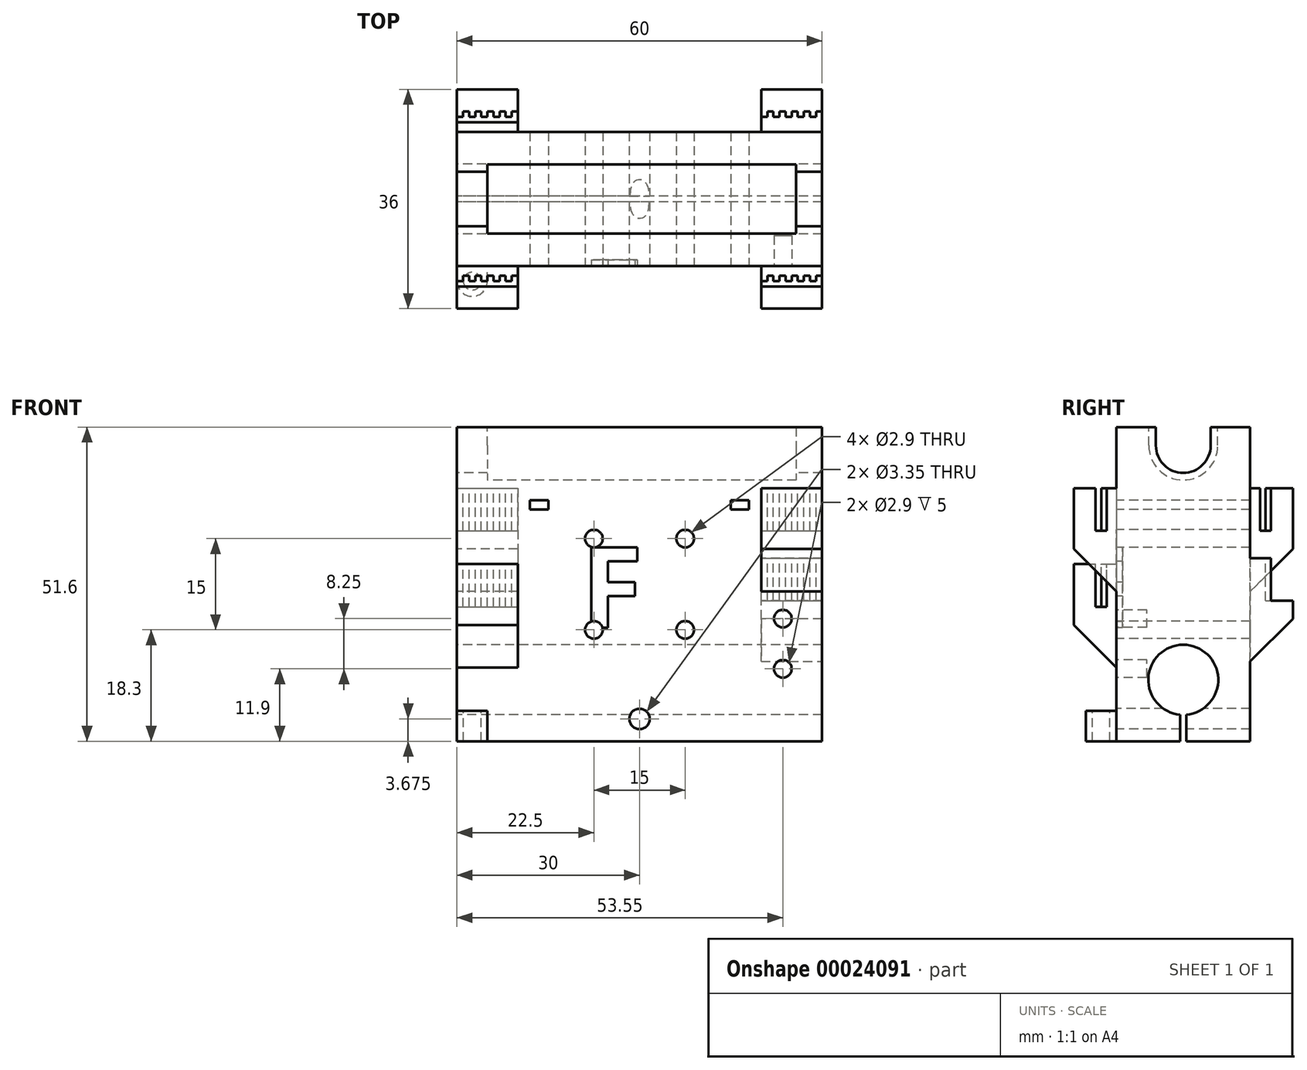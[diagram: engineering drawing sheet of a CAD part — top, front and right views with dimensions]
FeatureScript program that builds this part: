
annotation { "Feature Type Name" : "Feature", "Feature Type Description" : "" }
export const myFeature = defineFeature(function(context is Context, id is Id, definition is map)
    precondition{}
    {
        {
            var Q0;
            Q0=qCreatedBy(makeId("Top.planeOp"),FACE);
            var sketch = newSketch(context, id + "F0", { "sketchPlane" : qUnion([Q0])});
            skLineSegment(sketch, "E0.bottom", {"start": v(0, 0) * mm, "end": v(60, 0) * mm});
            skLineSegment(sketch, "E0.top", {"start": v(0, 22) * mm, "end": v(60, 22) * mm});
            skLineSegment(sketch, "E0.left", {"start": v(0, 0) * mm, "end": v(0, 22) * mm});
            skLineSegment(sketch, "E0.right", {"start": v(60, 0) * mm, "end": v(60, 22) * mm});
            skSolve(sketch);
        }
        {
            var Q0;
            Q0=qSketchRegion(id+"F0",true);
            extrude(context, id + "F1", {"entities" : qUnion([Q0]), "depth" : 51.6 * mm});
        }
        {
            var Q0;
            Q0=makeQuery(id+"F1.opExtrude","SWEPT_FACE",FACE,{"disambiguationData":[OSD([sQuery(id+"F0.wireOp",EDGE,"E0.left")])]});
            var sketch = newSketch(context, id + "F2", { "sketchPlane" : qUnion([Q0])});
            skCircle(sketch, "E1", {"center": v(-11, 10.1) * mm, "radius": 5.75 * mm});
            skCircle(sketch, "E2", {"center": v(-11, 48.6) * mm, "radius": 4.5 * mm});
            skLineSegment(sketch, "E3", {"start": v(-22, 48.6) * mm, "end": v(0, 48.6) * mm, "construction": true});
            skLineSegment(sketch, "E4", {"start": v(-15.5, 51.6) * mm, "end": v(-15.5, 48.6) * mm});
            skLineSegment(sketch, "E5", {"start": v(-6.5, 51.6) * mm, "end": v(-6.5, 48.6) * mm});
            skLineSegment(sketch, "E6", {"start": v(-22, 10.1) * mm, "end": v(0, 10.1) * mm, "construction": true});
            skLineSegment(sketch, "E7", {"start": v(-11, 10.1) * mm, "end": v(-11, 0) * mm, "construction": true});
            skLineSegment(sketch, "E8", {"start": v(-11, 0) * mm, "end": v(-11.5, 0) * mm});
            skLineSegment(sketch, "E9", {"start": v(-11.5, 0) * mm, "end": v(-11.5, 4.37) * mm});
            skLineSegment(sketch, "E10", {"start": v(-11.5, 4.37) * mm, "end": v(-10.5, 4.37) * mm});
            skLineSegment(sketch, "E11", {"start": v(-10.5, 4.37) * mm, "end": v(-10.5, 0) * mm});
            skLineSegment(sketch, "E12", {"start": v(-10.5, 0) * mm, "end": v(-11, 0) * mm});
            skLineSegment(sketch, "E13", {"start": v(-11, 15.85) * mm, "end": v(-11, 19.08) * mm});
            skLineSegment(sketch, "E14", {"start": v(-11, 19.08) * mm, "end": v(-7.6, 14.73) * mm});
            skLineSegment(sketch, "E15", {"start": v(-11, 19.08) * mm, "end": v(-14.4, 14.73) * mm});
            skCircle(sketch, "E16", {"center": v(-11, 48.6) * mm, "radius": 5.68 * mm});
            skLineSegment(sketch, "E17", {"start": v(-5.32, 48.6) * mm, "end": v(-5.32, 51.6) * mm});
            skLineSegment(sketch, "E18", {"start": v(-16.67, 48.6) * mm, "end": v(-16.67, 51.6) * mm});
            skSolve(sketch);
        }
        {
            var Q0;
            {var subQ0=sQuery(id+"F2.wireOp",EDGE,"E14");var subQ1=sQuery(id+"F2.wireOp",EDGE,"E1");var subQ3=makeQuery(id+"F2.imprint","INTERSECT",VERTEX,{"disambiguationData":[OD(0.0)],"derivedFrom":[subQ1,subQ0]});Q0=makeQuery(id+"F2.imprint","IMPRINT",FACE,{"disambiguationData":[TD([[makeQuery(id+"F2.imprint","IMPRINT",EDGE,{"disambiguationData":[TD([[subQ3,-1.0]])],"derivedFrom":subQ1}),1.0]])]});}
            var Q1;
            {var subQ0=sQuery(id+"F2.wireOp",EDGE,"E15");var subQ1=sQuery(id+"F2.wireOp",EDGE,"E1");var subQ3=makeQuery(id+"F2.imprint","INTERSECT",VERTEX,{"disambiguationData":[OD(0.0)],"derivedFrom":[subQ1,subQ0]});Q1=makeQuery(id+"F2.imprint","IMPRINT",FACE,{"disambiguationData":[TD([[makeQuery(id+"F2.imprint","IMPRINT",EDGE,{"disambiguationData":[TD([[subQ3,1.0]])],"derivedFrom":subQ1}),1.0]])]});}
            var Q2;
            Q2=makeQuery(id+"F2.imprint","IMPRINT",FACE,{"disambiguationData":[TD([[makeQuery(id+"F2.imprint","IMPRINT",EDGE,{"derivedFrom":sQuery(id+"F2.wireOp",EDGE,"E8")}),-1.0]])]});
            var Q3;
            {var subQ0=sQuery(id+"F2.wireOp",EDGE,"E10");Q3=makeQuery(id+"F2.imprint","IMPRINT",FACE,{"disambiguationData":[TD([[makeQuery(id+"F2.imprint","IMPRINT",EDGE,{"derivedFrom":subQ0}),-1.0]])]});}
            var Q4;
            {var subQ7=sQuery(id+"F2.wireOp",EDGE,"E10");Q4=makeQuery(id+"F2.imprint","IMPRINT",FACE,{"disambiguationData":[TD([[makeQuery(id+"F2.imprint","IMPRINT",EDGE,{"derivedFrom":subQ7}),1.0]])]});}
            var Q5;
            {var subQ3=sQuery(id+"F2.wireOp",EDGE,"E5");Q5=makeQuery(id+"F2.imprint","IMPRINT",FACE,{"disambiguationData":[TD([[makeQuery(id+"F2.imprint","IMPRINT",EDGE,{"derivedFrom":subQ3}),-1.0]])]});}
            var Q6;
            {var subQ0=sQuery(id+"F2.wireOp",EDGE,"E4");Q6=makeQuery(id+"F2.imprint","IMPRINT",FACE,{"disambiguationData":[TD([[makeQuery(id+"F2.imprint","IMPRINT",EDGE,{"derivedFrom":subQ0}),1.0]])]});}
            var Q7;
            {var subQ0=sQuery(id+"F2.wireOp",EDGE,"E4");Q7=makeQuery(id+"F2.imprint","IMPRINT",FACE,{"disambiguationData":[TD([[makeQuery(id+"F2.imprint","IMPRINT",EDGE,{"derivedFrom":subQ0}),1.0]])]});}
            var Q8;
            {var subQ3=sQuery(id+"F2.wireOp",EDGE,"E5");Q8=makeQuery(id+"F2.imprint","IMPRINT",FACE,{"disambiguationData":[TD([[makeQuery(id+"F2.imprint","IMPRINT",EDGE,{"derivedFrom":subQ3}),-1.0]])]});}
            var Q9;
            {var subQ1=sQuery(id+"F2.wireOp",EDGE,"E2");var subQ4=makeQuery(id+"F2.imprint","INTERSECT",VERTEX,{"derivedFrom":[subQ1,sQuery(id+"F2.wireOp",EDGE,"E5")]});Q9=makeQuery(id+"F2.imprint","IMPRINT",FACE,{"disambiguationData":[TD([[makeQuery(id+"F2.imprint","IMPRINT",EDGE,{"disambiguationData":[TD([[subQ4,-1.0]])],"derivedFrom":subQ1}),1.0]])]});}
            extrude(context, id + "F3", {"entities" : qUnion([Q0, Q1, Q2, Q3, Q4, Q5, Q6, Q7, Q8, Q9]), "operationType" : NewBodyOperationType.REMOVE, "endBound" : BoundingType.THROUGH_ALL, "oppositeDirection" : true, "depth" : 25 * mm});
        }
        {
            var Q0;
            {var subQ3=sQuery(id+"F2.wireOp",EDGE,"E4");Q0=makeQuery(id+"F2.imprint","IMPRINT",FACE,{"disambiguationData":[TD([[makeQuery(id+"F2.imprint","IMPRINT",EDGE,{"derivedFrom":subQ3}),-1.0]])]});}
            var Q1;
            {var subQ3=sQuery(id+"F2.wireOp",EDGE,"E18");Q1=makeQuery(id+"F2.imprint","IMPRINT",FACE,{"disambiguationData":[TD([[makeQuery(id+"F2.imprint","IMPRINT",EDGE,{"derivedFrom":subQ3}),-1.0]])]});}
            var Q2;
            {var subQ3=sQuery(id+"F2.wireOp",EDGE,"E17");Q2=makeQuery(id+"F2.imprint","IMPRINT",FACE,{"disambiguationData":[TD([[makeQuery(id+"F2.imprint","IMPRINT",EDGE,{"derivedFrom":subQ3}),1.0]])]});}
            extrude(context, id + "F4", {"entities" : qUnion([Q0, Q1, Q2]), "operationType" : NewBodyOperationType.REMOVE, "oppositeDirection" : true, "depth" : 55.75 * mm});
        }
        {
            var Q0;
            {var subQ3=sQuery(id+"F2.wireOp",EDGE,"E4");Q0=makeQuery(id+"F2.imprint","IMPRINT",FACE,{"disambiguationData":[TD([[makeQuery(id+"F2.imprint","IMPRINT",EDGE,{"derivedFrom":subQ3}),-1.0]])]});}
            var Q1;
            {var subQ3=sQuery(id+"F2.wireOp",EDGE,"E18");Q1=makeQuery(id+"F2.imprint","IMPRINT",FACE,{"disambiguationData":[TD([[makeQuery(id+"F2.imprint","IMPRINT",EDGE,{"derivedFrom":subQ3}),-1.0]])]});}
            var Q2;
            {var subQ3=sQuery(id+"F2.wireOp",EDGE,"E17");Q2=makeQuery(id+"F2.imprint","IMPRINT",FACE,{"disambiguationData":[TD([[makeQuery(id+"F2.imprint","IMPRINT",EDGE,{"derivedFrom":subQ3}),1.0]])]});}
            extrude(context, id + "F5", {"entities" : qUnion([Q0, Q1, Q2]), "operationType" : NewBodyOperationType.ADD, "oppositeDirection" : true, "depth" : 32.75 * mm});
        }
        {
            var Q0;
            {var subQ3=sQuery(id+"F2.wireOp",EDGE,"E4");Q0=makeQuery(id+"F2.imprint","IMPRINT",FACE,{"disambiguationData":[TD([[makeQuery(id+"F2.imprint","IMPRINT",EDGE,{"derivedFrom":subQ3}),-1.0]])]});}
            var Q1;
            {var subQ3=sQuery(id+"F2.wireOp",EDGE,"E18");Q1=makeQuery(id+"F2.imprint","IMPRINT",FACE,{"disambiguationData":[TD([[makeQuery(id+"F2.imprint","IMPRINT",EDGE,{"derivedFrom":subQ3}),-1.0]])]});}
            var Q2;
            {var subQ3=sQuery(id+"F2.wireOp",EDGE,"E17");Q2=makeQuery(id+"F2.imprint","IMPRINT",FACE,{"disambiguationData":[TD([[makeQuery(id+"F2.imprint","IMPRINT",EDGE,{"derivedFrom":subQ3}),1.0]])]});}
            extrude(context, id + "F6", {"entities" : qUnion([Q0, Q1, Q2]), "operationType" : NewBodyOperationType.REMOVE, "oppositeDirection" : true, "depth" : 34.25 * mm});
        }
        {
            var Q0;
            {var subQ3=sQuery(id+"F2.wireOp",EDGE,"E4");Q0=makeQuery(id+"F2.imprint","IMPRINT",FACE,{"disambiguationData":[TD([[makeQuery(id+"F2.imprint","IMPRINT",EDGE,{"derivedFrom":subQ3}),-1.0]])]});}
            var Q1;
            {var subQ3=sQuery(id+"F2.wireOp",EDGE,"E18");Q1=makeQuery(id+"F2.imprint","IMPRINT",FACE,{"disambiguationData":[TD([[makeQuery(id+"F2.imprint","IMPRINT",EDGE,{"derivedFrom":subQ3}),-1.0]])]});}
            var Q2;
            {var subQ3=sQuery(id+"F2.wireOp",EDGE,"E17");Q2=makeQuery(id+"F2.imprint","IMPRINT",FACE,{"disambiguationData":[TD([[makeQuery(id+"F2.imprint","IMPRINT",EDGE,{"derivedFrom":subQ3}),1.0]])]});}
            extrude(context, id + "F7", {"entities" : qUnion([Q0, Q1, Q2]), "operationType" : NewBodyOperationType.ADD, "oppositeDirection" : true, "depth" : 5 * mm});
        }
        {
            var Q0;
            Q0=makeQuery(id+"F1.opExtrude","SWEPT_FACE",FACE,{"disambiguationData":[OSD([sQuery(id+"F0.wireOp",EDGE,"E0.bottom")])]});
            var sketch = newSketch(context, id + "F8", { "sketchPlane" : qUnion([Q0])});
            skLineSegment(sketch, "E19.bottom", {"start": v(0, 29.1) * mm, "end": v(10, 29.1) * mm});
            skLineSegment(sketch, "E19.top", {"start": v(0, 9.1) * mm, "end": v(10, 9.1) * mm});
            skLineSegment(sketch, "E19.left", {"start": v(0, 29.1) * mm, "end": v(0, 9.1) * mm});
            skLineSegment(sketch, "E19.right", {"start": v(10, 29.1) * mm, "end": v(10, 9.1) * mm});
            skLineSegment(sketch, "E20.bottom", {"start": v(60, 41.6) * mm, "end": v(50, 41.6) * mm});
            skLineSegment(sketch, "E20.top", {"start": v(60, 21.6) * mm, "end": v(50, 21.6) * mm});
            skLineSegment(sketch, "E20.left", {"start": v(60, 41.6) * mm, "end": v(60, 21.6) * mm});
            skLineSegment(sketch, "E20.right", {"start": v(50, 41.6) * mm, "end": v(50, 21.6) * mm});
            skPoint(sketch, "E21", {"position": v(0, 48.6) * mm});
            skPoint(sketch, "E22", {"position": v(0, 8.6) * mm});
            skSolve(sketch);
        }
        {
            var Q0;
            Q0=qSketchRegion(id+"F8",true);
            extrude(context, id + "F9", {"entities" : qUnion([Q0]), "operationType" : NewBodyOperationType.ADD, "depth" : 7 * mm});
        }
        {
            var Q0;
            Q0=makeQuery(id+"F9.opExtrude","CAP_EDGE",EDGE,{"disambiguationData":[OSD([sQuery(id+"F8.wireOp",EDGE,"E19.top")])],"isStart":false});
            var Q1;
            Q1=makeQuery(id+"F9.opExtrude","CAP_EDGE",EDGE,{"disambiguationData":[OSD([sQuery(id+"F8.wireOp",EDGE,"E20.top")])],"isStart":false});
            chamfer(context, id + "F10", {"entities" : qUnion([Q0, Q1]), "width" : 10 * mm, "tangentPropagation" : true});
        }
        {
            var Q0;
            Q0=makeQuery(id+"F9.opExtrude","SWEPT_FACE",FACE,{"disambiguationData":[OSD([sQuery(id+"F8.wireOp",EDGE,"E19.bottom")])]});
            var sketch = newSketch(context, id + "F11", { "sketchPlane" : qUnion([Q0])});
            skLineSegment(sketch, "E23", {"start": v(-935.9, 0) * mm, "end": v(-935.88, -4.54) * mm});
            skLineSegment(sketch, "E24.left", {"start": v(0, -3.4) * mm, "end": v(0, -1.6) * mm});
            skLineSegment(sketch, "E25", {"start": v(6, -2.5) * mm, "end": v(7, -2.5) * mm});
            skLineSegment(sketch, "E26", {"start": v(4, -2.5) * mm, "end": v(5, -2.5) * mm});
            skLineSegment(sketch, "E27", {"start": v(0, -2.5) * mm, "end": v(1, -2.5) * mm});
            skLineSegment(sketch, "E28", {"start": v(7, -1.6) * mm, "end": v(8, -1.6) * mm});
            skLineSegment(sketch, "E29", {"start": v(2, -2.5) * mm, "end": v(3, -2.5) * mm});
            skLineSegment(sketch, "E30", {"start": v(3, -1.6) * mm, "end": v(4, -1.6) * mm});
            skLineSegment(sketch, "E31", {"start": v(8, -2.5) * mm, "end": v(9, -2.5) * mm});
            skLineSegment(sketch, "E32", {"start": v(8, -1.6) * mm, "end": v(8, -2.5) * mm});
            skLineSegment(sketch, "E33", {"start": v(9, -2.5) * mm, "end": v(9, -1.6) * mm});
            skLineSegment(sketch, "E34", {"start": v(10, -1.6) * mm, "end": v(10, -2.5) * mm});
            skLineSegment(sketch, "E35", {"start": v(6, -1.6) * mm, "end": v(6, -2.5) * mm});
            skLineSegment(sketch, "E36", {"start": v(2, -1.6) * mm, "end": v(2, -2.5) * mm});
            skLineSegment(sketch, "E37", {"start": v(1, -1.6) * mm, "end": v(2, -1.6) * mm});
            skLineSegment(sketch, "E38", {"start": v(1, -2.5) * mm, "end": v(1, -1.6) * mm});
            skLineSegment(sketch, "E39", {"start": v(9, -1.6) * mm, "end": v(10, -1.6) * mm});
            skLineSegment(sketch, "E40", {"start": v(5, -1.6) * mm, "end": v(6, -1.6) * mm});
            skLineSegment(sketch, "E41", {"start": v(5, -2.5) * mm, "end": v(5, -1.6) * mm});
            skLineSegment(sketch, "E42", {"start": v(3, -2.5) * mm, "end": v(3, -1.6) * mm});
            skLineSegment(sketch, "E43", {"start": v(4, -1.6) * mm, "end": v(4, -2.5) * mm});
            skLineSegment(sketch, "E44", {"start": v(7, -2.5) * mm, "end": v(7, -1.6) * mm});
            skLineSegment(sketch, "E45", {"start": v(0, -1.6) * mm, "end": v(0, -2.5) * mm});
            skLineSegment(sketch, "E46", {"start": v(10, -2.5) * mm, "end": v(10, -3.4) * mm});
            skLineSegment(sketch, "E47", {"start": v(0, -3.4) * mm, "end": v(10, -3.4) * mm});
            skLineSegment(sketch, "E48", {"start": v(5.3, -1.6) * mm, "end": v(5.3, 0) * mm});
            skSolve(sketch);
        }
        {
            var Q0;
            Q0=qSketchRegion(id+"F11",true);
            extrude(context, id + "F12", {"entities" : qUnion([Q0]), "operationType" : NewBodyOperationType.REMOVE, "oppositeDirection" : true, "depth" : 7 * mm});
        }
        {
            var Q0;
            Q0=makeQuery(id+"F9.opExtrude","SWEPT_FACE",FACE,{"disambiguationData":[OSD([sQuery(id+"F8.wireOp",EDGE,"E20.bottom")])]});
            var sketch = newSketch(context, id + "F13", { "sketchPlane" : qUnion([Q0])});
            skLineSegment(sketch, "E49.left", {"start": v(50, -3.4) * mm, "end": v(50, -1.6) * mm});
            skLineSegment(sketch, "E50", {"start": v(56, -2.5) * mm, "end": v(57, -2.5) * mm});
            skLineSegment(sketch, "E51", {"start": v(54, -2.5) * mm, "end": v(55, -2.5) * mm});
            skLineSegment(sketch, "E52", {"start": v(50, -2.5) * mm, "end": v(51, -2.5) * mm});
            skLineSegment(sketch, "E53", {"start": v(57, -1.6) * mm, "end": v(58, -1.6) * mm});
            skLineSegment(sketch, "E54", {"start": v(52, -2.5) * mm, "end": v(53, -2.5) * mm});
            skLineSegment(sketch, "E55", {"start": v(53, -1.6) * mm, "end": v(54, -1.6) * mm});
            skLineSegment(sketch, "E56", {"start": v(58, -2.5) * mm, "end": v(59, -2.5) * mm});
            skLineSegment(sketch, "E57", {"start": v(58, -1.6) * mm, "end": v(58, -2.5) * mm});
            skLineSegment(sketch, "E58", {"start": v(59, -2.5) * mm, "end": v(59, -1.6) * mm});
            skLineSegment(sketch, "E59", {"start": v(60, -1.6) * mm, "end": v(60, -2.5) * mm});
            skLineSegment(sketch, "E60", {"start": v(56, -1.6) * mm, "end": v(56, -2.5) * mm});
            skLineSegment(sketch, "E61", {"start": v(52, -1.6) * mm, "end": v(52, -2.5) * mm});
            skLineSegment(sketch, "E62", {"start": v(51, -1.6) * mm, "end": v(52, -1.6) * mm});
            skLineSegment(sketch, "E63", {"start": v(51, -2.5) * mm, "end": v(51, -1.6) * mm});
            skLineSegment(sketch, "E64", {"start": v(59, -1.6) * mm, "end": v(60, -1.6) * mm});
            skLineSegment(sketch, "E65", {"start": v(55, -1.6) * mm, "end": v(56, -1.6) * mm});
            skLineSegment(sketch, "E66", {"start": v(55, -2.5) * mm, "end": v(55, -1.6) * mm});
            skLineSegment(sketch, "E67", {"start": v(53, -2.5) * mm, "end": v(53, -1.6) * mm});
            skLineSegment(sketch, "E68", {"start": v(54, -1.6) * mm, "end": v(54, -2.5) * mm});
            skLineSegment(sketch, "E69", {"start": v(57, -2.5) * mm, "end": v(57, -1.6) * mm});
            skLineSegment(sketch, "E70", {"start": v(50, -1.6) * mm, "end": v(50, -2.5) * mm});
            skLineSegment(sketch, "E71", {"start": v(60, -2.5) * mm, "end": v(60, -3.4) * mm});
            skLineSegment(sketch, "E72", {"start": v(50, -3.4) * mm, "end": v(60, -3.4) * mm});
            skLineSegment(sketch, "E73", {"start": v(55.23, -1.6) * mm, "end": v(55.23, 0) * mm});
            skSolve(sketch);
        }
        {
            var Q0;
            Q0=qSketchRegion(id+"F13",true);
            extrude(context, id + "F14", {"entities" : qUnion([Q0]), "operationType" : NewBodyOperationType.REMOVE, "oppositeDirection" : true, "depth" : 7 * mm});
        }
        {
            var Q0;
            Q0=makeQuery(id+"F1.opExtrude","SWEPT_FACE",FACE,{"disambiguationData":[OSD([sQuery(id+"F0.wireOp",EDGE,"E0.top")])]});
            var sketch = newSketch(context, id + "F15", { "sketchPlane" : qUnion([Q0])});
            skLineSegment(sketch, "E74.bottom", {"start": v(-60, 10.1) * mm, "end": v(-50, 10.1) * mm});
            skLineSegment(sketch, "E74.top", {"start": v(-60, 30.1) * mm, "end": v(-50, 30.1) * mm});
            skLineSegment(sketch, "E74.left", {"start": v(-60, 10.1) * mm, "end": v(-60, 30.1) * mm});
            skLineSegment(sketch, "E74.right", {"start": v(-50, 10.1) * mm, "end": v(-50, 30.1) * mm});
            skLineSegment(sketch, "E75.bottom", {"start": v(0, 41.6) * mm, "end": v(-10, 41.6) * mm});
            skLineSegment(sketch, "E75.top", {"start": v(0, 21.6) * mm, "end": v(-10, 21.6) * mm});
            skLineSegment(sketch, "E75.left", {"start": v(0, 41.6) * mm, "end": v(0, 21.6) * mm});
            skLineSegment(sketch, "E75.right", {"start": v(-10, 41.6) * mm, "end": v(-10, 21.6) * mm});
            skSolve(sketch);
        }
        {
            var Q0;
            Q0=qSketchRegion(id+"F15",true);
            extrude(context, id + "F16", {"entities" : qUnion([Q0]), "operationType" : NewBodyOperationType.ADD, "depth" : 7 * mm});
        }
        {
            var Q0;
            Q0=makeQuery(id+"F16.opExtrude","SWEPT_FACE",FACE,{"disambiguationData":[OSD([sQuery(id+"F15.wireOp",EDGE,"E74.top")])]});
            var sketch = newSketch(context, id + "F17", { "sketchPlane" : qUnion([Q0])});
            skLineSegment(sketch, "E76.left", {"start": v(50, 23.6) * mm, "end": v(50, 25.4) * mm});
            skLineSegment(sketch, "E77", {"start": v(56, 24.5) * mm, "end": v(57, 24.5) * mm});
            skLineSegment(sketch, "E78", {"start": v(54, 24.5) * mm, "end": v(55, 24.5) * mm});
            skLineSegment(sketch, "E79", {"start": v(50, 24.5) * mm, "end": v(51, 24.5) * mm});
            skLineSegment(sketch, "E80", {"start": v(57, 25.4) * mm, "end": v(58, 25.4) * mm});
            skLineSegment(sketch, "E81", {"start": v(52, 24.5) * mm, "end": v(53, 24.5) * mm});
            skLineSegment(sketch, "E82", {"start": v(53, 25.4) * mm, "end": v(54, 25.4) * mm});
            skLineSegment(sketch, "E83", {"start": v(58, 24.5) * mm, "end": v(59, 24.5) * mm});
            skLineSegment(sketch, "E84", {"start": v(58, 25.4) * mm, "end": v(58, 24.5) * mm});
            skLineSegment(sketch, "E85", {"start": v(59, 24.5) * mm, "end": v(59, 25.4) * mm});
            skLineSegment(sketch, "E86", {"start": v(60, 25.4) * mm, "end": v(60, 24.5) * mm});
            skLineSegment(sketch, "E87", {"start": v(56, 25.4) * mm, "end": v(56, 24.5) * mm});
            skLineSegment(sketch, "E88", {"start": v(52, 25.4) * mm, "end": v(52, 24.5) * mm});
            skLineSegment(sketch, "E89", {"start": v(51, 25.4) * mm, "end": v(52, 25.4) * mm});
            skLineSegment(sketch, "E90", {"start": v(51, 24.5) * mm, "end": v(51, 25.4) * mm});
            skLineSegment(sketch, "E91", {"start": v(59, 25.4) * mm, "end": v(60, 25.4) * mm});
            skLineSegment(sketch, "E92", {"start": v(55, 25.4) * mm, "end": v(56, 25.4) * mm});
            skLineSegment(sketch, "E93", {"start": v(55, 24.5) * mm, "end": v(55, 25.4) * mm});
            skLineSegment(sketch, "E94", {"start": v(53, 24.5) * mm, "end": v(53, 25.4) * mm});
            skLineSegment(sketch, "E95", {"start": v(54, 25.4) * mm, "end": v(54, 24.5) * mm});
            skLineSegment(sketch, "E96", {"start": v(57, 24.5) * mm, "end": v(57, 25.4) * mm});
            skLineSegment(sketch, "E97", {"start": v(50, 25.4) * mm, "end": v(50, 24.5) * mm});
            skLineSegment(sketch, "E98", {"start": v(60, 24.5) * mm, "end": v(60, 23.6) * mm});
            skLineSegment(sketch, "E99", {"start": v(50, 23.6) * mm, "end": v(60, 23.6) * mm});
            skLineSegment(sketch, "E100", {"start": v(55, 23.6) * mm, "end": v(55, 22) * mm});
            skSolve(sketch);
        }
        {
            var Q0;
            {var subQ4=sQuery(id+"F17.wireOp",EDGE,"E76.left");Q0=makeQuery(id+"F17.imprint","IMPRINT",FACE,{"disambiguationData":[TD([[makeQuery(id+"F17.imprint","IMPRINT",EDGE,{"derivedFrom":subQ4}),1.0]])]});}
            extrude(context, id + "F18", {"entities" : qUnion([Q0]), "operationType" : NewBodyOperationType.REMOVE, "oppositeDirection" : true, "depth" : 7 * mm});
        }
        {
            var Q0;
            Q0=makeQuery(id+"F16.opExtrude","SWEPT_FACE",FACE,{"disambiguationData":[OSD([sQuery(id+"F15.wireOp",EDGE,"E75.bottom")])]});
            var sketch = newSketch(context, id + "F19", { "sketchPlane" : qUnion([Q0])});
            skLineSegment(sketch, "E101", {"start": v(6, 24.5) * mm, "end": v(7, 24.5) * mm});
            skLineSegment(sketch, "E102", {"start": v(4, 24.5) * mm, "end": v(5, 24.5) * mm});
            skLineSegment(sketch, "E103", {"start": v(0, 24.5) * mm, "end": v(1, 24.5) * mm});
            skLineSegment(sketch, "E104", {"start": v(7, 25.4) * mm, "end": v(8, 25.4) * mm});
            skLineSegment(sketch, "E105", {"start": v(2, 24.5) * mm, "end": v(3, 24.5) * mm});
            skLineSegment(sketch, "E106", {"start": v(3, 25.4) * mm, "end": v(4, 25.4) * mm});
            skLineSegment(sketch, "E107", {"start": v(8, 24.5) * mm, "end": v(9, 24.5) * mm});
            skLineSegment(sketch, "E108", {"start": v(8, 25.4) * mm, "end": v(8, 24.5) * mm});
            skLineSegment(sketch, "E109", {"start": v(9, 24.5) * mm, "end": v(9, 25.4) * mm});
            skLineSegment(sketch, "E110", {"start": v(10, 25.4) * mm, "end": v(10, 24.5) * mm});
            skLineSegment(sketch, "E111", {"start": v(6, 25.4) * mm, "end": v(6, 24.5) * mm});
            skLineSegment(sketch, "E112", {"start": v(2, 25.4) * mm, "end": v(2, 24.5) * mm});
            skLineSegment(sketch, "E113", {"start": v(1, 25.4) * mm, "end": v(2, 25.4) * mm});
            skLineSegment(sketch, "E114", {"start": v(1, 24.5) * mm, "end": v(1, 25.4) * mm});
            skLineSegment(sketch, "E115", {"start": v(9, 25.4) * mm, "end": v(10, 25.4) * mm});
            skLineSegment(sketch, "E116", {"start": v(5, 25.4) * mm, "end": v(6, 25.4) * mm});
            skLineSegment(sketch, "E117", {"start": v(5, 24.5) * mm, "end": v(5, 25.4) * mm});
            skLineSegment(sketch, "E118", {"start": v(3, 24.5) * mm, "end": v(3, 25.4) * mm});
            skLineSegment(sketch, "E119", {"start": v(4, 25.4) * mm, "end": v(4, 24.5) * mm});
            skLineSegment(sketch, "E120", {"start": v(7, 24.5) * mm, "end": v(7, 25.4) * mm});
            skLineSegment(sketch, "E121", {"start": v(10, 24.5) * mm, "end": v(10, 23.6) * mm});
            skLineSegment(sketch, "E122", {"start": v(0, 23.6) * mm, "end": v(10, 23.6) * mm});
            skLineSegment(sketch, "E123", {"start": v(5, 23.6) * mm, "end": v(5, 22) * mm});
            skLineSegment(sketch, "E124", {"start": v(0, 23.6) * mm, "end": v(0, 24.5) * mm});
            skSolve(sketch);
        }
        {
            var Q0;
            Q0=makeQuery(id+"F19.imprint","IMPRINT",FACE,{"disambiguationData":[TD([[makeQuery(id+"F19.imprint","IMPRINT",EDGE,{"derivedFrom":sQuery(id+"F19.wireOp",EDGE,"E101")}),-1.0]])]});
            extrude(context, id + "F20", {"entities" : qUnion([Q0]), "operationType" : NewBodyOperationType.REMOVE, "oppositeDirection" : true, "depth" : 7 * mm});
        }
        {
            var Q0;
            Q0=makeQuery(id+"F16.opExtrude","CAP_EDGE",EDGE,{"disambiguationData":[OSD([sQuery(id+"F15.wireOp",EDGE,"E75.top")])],"isStart":false});
            var Q1;
            Q1=makeQuery(id+"F16.opExtrude","CAP_EDGE",EDGE,{"disambiguationData":[OSD([sQuery(id+"F15.wireOp",EDGE,"E74.bottom")])],"isStart":false});
            chamfer(context, id + "F21", {"entities" : qUnion([Q0, Q1]), "width" : 10 * mm, "tangentPropagation" : true});
        }
        {
            var Q0;
            Q0=makeQuery(id+"F1.opExtrude","SWEPT_FACE",FACE,{"disambiguationData":[OSD([sQuery(id+"F0.wireOp",EDGE,"E0.bottom")])]});
            var sketch = newSketch(context, id + "F22", { "sketchPlane" : qUnion([Q0])});
            skCircle(sketch, "E125", {"center": v(22.5, 33.3) * mm, "radius": 1.45 * mm});
            skCircle(sketch, "E126", {"center": v(37.5, 33.3) * mm, "radius": 1.45 * mm});
            skCircle(sketch, "E127", {"center": v(22.5, 18.3) * mm, "radius": 1.45 * mm});
            skCircle(sketch, "E128", {"center": v(37.5, 18.3) * mm, "radius": 1.45 * mm});
            skLineSegment(sketch, "E129", {"start": v(22.5, 33.3) * mm, "end": v(0, 33.3) * mm});
            skLineSegment(sketch, "E130", {"start": v(37.5, 18.3) * mm, "end": v(60, 18.3) * mm});
            skLineSegment(sketch, "E131", {"start": v(37.5, 33.3) * mm, "end": v(37.5, 51.6) * mm});
            skLineSegment(sketch, "E132", {"start": v(22.5, 18.3) * mm, "end": v(22.5, 0) * mm});
            skCircle(sketch, "E133", {"center": v(30, 3.68) * mm, "radius": 1.68 * mm});
            skLineSegment(sketch, "E134", {"start": v(30, 0) * mm, "end": v(30, 13.82) * mm, "construction": true});
            skSolve(sketch);
        }
        {
            var Q0;
            Q0=qSketchRegion(id+"F22",true);
            var Q1;
            Q1=makeQuery(id+"F22.imprint","IMPRINT",FACE,{"disambiguationData":[TD([[makeQuery(id+"F22.imprint","IMPRINT",EDGE,{"derivedFrom":sQuery(id+"F22.wireOp",EDGE,"E125")}),1.0]])]});
            var Q2;
            Q2=makeQuery(id+"F22.imprint","IMPRINT",FACE,{"disambiguationData":[TD([[makeQuery(id+"F22.imprint","IMPRINT",EDGE,{"derivedFrom":sQuery(id+"F22.wireOp",EDGE,"E126")}),1.0]])]});
            var Q3;
            Q3=makeQuery(id+"F22.imprint","IMPRINT",FACE,{"disambiguationData":[TD([[makeQuery(id+"F22.imprint","IMPRINT",EDGE,{"derivedFrom":sQuery(id+"F22.wireOp",EDGE,"E128")}),1.0]])]});
            var Q4;
            Q4=makeQuery(id+"F22.imprint","IMPRINT",FACE,{"disambiguationData":[TD([[makeQuery(id+"F22.imprint","IMPRINT",EDGE,{"derivedFrom":sQuery(id+"F22.wireOp",EDGE,"E127")}),1.0]])]});
            extrude(context, id + "F23", {"entities" : qUnion([Q0, Q1, Q2, Q3, Q4]), "operationType" : NewBodyOperationType.REMOVE, "endBound" : BoundingType.THROUGH_ALL, "oppositeDirection" : true, "depth" : 25 * mm});
        }
        {
            var Q0;
            Q0=makeQuery(id+"F1.opExtrude","SWEPT_FACE",FACE,{"disambiguationData":[OSD([sQuery(id+"F0.wireOp",EDGE,"E0.bottom")])]});
            var sketch = newSketch(context, id + "F24", { "sketchPlane" : qUnion([Q0])});
            skCircle(sketch, "E135", {"center": v(53.55, 20.15) * mm, "radius": 1.45 * mm});
            skCircle(sketch, "E136", {"center": v(53.55, 11.9) * mm, "radius": 1.45 * mm});
            skSolve(sketch);
        }
        {
            var Q0;
            Q0=qSketchRegion(id+"F24",true);
            extrude(context, id + "F25", {"entities" : qUnion([Q0]), "operationType" : NewBodyOperationType.REMOVE, "oppositeDirection" : true, "depth" : 5 * mm});
        }
        {
            var Q0;
            Q0=makeQuery(id+"F1.opExtrude","SWEPT_FACE",FACE,{"disambiguationData":[OSD([sQuery(id+"F0.wireOp",EDGE,"E0.bottom")])]});
            var sketch = newSketch(context, id + "F26", { "sketchPlane" : qUnion([Q0])});
            skText(sketch, "E137", { "text": "F", "fontName": "OpenSans-Bold.ttf"});
            skLineSegment(sketch, "E138", {"start": v(22.5, 33.3) * mm, "end": v(22.5, 18.3) * mm, "construction": true});
            skLineSegment(sketch, "E139", {"start": v(22.5, 18.3) * mm, "end": v(37.5, 18.3) * mm, "construction": true});
            skLineSegment(sketch, "E140", {"start": v(37.5, 18.3) * mm, "end": v(37.5, 33.3) * mm, "construction": true});
            skLineSegment(sketch, "E141", {"start": v(37.5, 33.3) * mm, "end": v(22.5, 33.3) * mm, "construction": true});
            skLineSegment(sketch, "E142", {"start": v(22.5, 25.8) * mm, "end": v(25.4, 25.8) * mm, "construction": true});
            skLineSegment(sketch, "E143", {"start": v(34.6, 25.8) * mm, "end": v(37.5, 25.8) * mm, "construction": true});
            skLineSegment(sketch, "E144", {"start": v(30, 19.16) * mm, "end": v(30, 18.3) * mm, "construction": true});
            skLineSegment(sketch, "E145", {"start": v(30, 33.3) * mm, "end": v(30, 32.44) * mm, "construction": true});
            const initialGuessF26  = {"E137": [0.0204, 0.01866, 1, 0, 0.01328]};
            skSetInitialGuess(sketch, initialGuessF26);
            skSolve(sketch);
        }
        {
            var Q0;
            Q0=qSketchRegion(id+"F26",true);
            extrude(context, id + "F27", {"entities" : qUnion([Q0]), "operationType" : NewBodyOperationType.REMOVE, "oppositeDirection" : true, "depth" : 1 * mm});
        }
        {
            var Q0;
            Q0=makeQuery(id+"F1.opExtrude","SWEPT_FACE",FACE,{"disambiguationData":[OSD([sQuery(id+"F0.wireOp",EDGE,"E0.bottom")])]});
            var sketch = newSketch(context, id + "F28", { "sketchPlane" : qUnion([Q0])});
            skLineSegment(sketch, "E146.bottom", {"start": v(0, 0) * mm, "end": v(5, 0) * mm});
            skLineSegment(sketch, "E146.top", {"start": v(0, 5) * mm, "end": v(5, 5) * mm});
            skLineSegment(sketch, "E146.left", {"start": v(0, 0) * mm, "end": v(0, 5) * mm});
            skLineSegment(sketch, "E146.right", {"start": v(5, 0) * mm, "end": v(5, 5) * mm});
            skSolve(sketch);
        }
        {
            var Q0;
            Q0=qSketchRegion(id+"F28",true);
            extrude(context, id + "F29", {"entities" : qUnion([Q0]), "operationType" : NewBodyOperationType.ADD, "depth" : 5 * mm});
        }
        {
            var Q0;
            Q0=makeQuery(id+"F29.opExtrude","SWEPT_FACE",FACE,{"disambiguationData":[OSD([sQuery(id+"F28.wireOp",EDGE,"E146.top")])]});
            var sketch = newSketch(context, id + "F30", { "sketchPlane" : qUnion([Q0])});
            skCircle(sketch, "E147", {"center": v(2.5, -2.5) * mm, "radius": 1.45 * mm});
            skLineSegment(sketch, "E148", {"start": v(0, -2.5) * mm, "end": v(5, -2.5) * mm});
            skSolve(sketch);
        }
        {
            var Q0;
            Q0=qSketchRegion(id+"F30",true);
            extrude(context, id + "F31", {"entities" : qUnion([Q0]), "operationType" : NewBodyOperationType.REMOVE, "oppositeDirection" : true, "depth" : 25 * mm});
        }
        {
            var Q0;
            Q0=makeQuery(id+"F29.opExtrude","CAP_EDGE",EDGE,{"disambiguationData":[OSD([sQuery(id+"F28.wireOp",EDGE,"E146.left")])],"isStart":false});
            var Q1;
            Q1=makeQuery(id+"F29.opExtrude","CAP_EDGE",EDGE,{"disambiguationData":[OSD([sQuery(id+"F28.wireOp",EDGE,"E146.right")])],"isStart":false});
            fillet(context, id + "F32", {"entities" : qUnion([Q0, Q1]), "radius" : 2.5 * mm, "tangentPropagation" : true, "allowEdgeOverflow" : false});
        }
        {
            var Q0;
            Q0=makeQuery(id+"F1.opExtrude","SWEPT_FACE",FACE,{"disambiguationData":[OSD([sQuery(id+"F0.wireOp",EDGE,"E0.bottom")])]});
            var sketch = newSketch(context, id + "F33", { "sketchPlane" : qUnion([Q0])});
            skLineSegment(sketch, "E149.bottom", {"start": v(12, 39.6) * mm, "end": v(15, 39.6) * mm});
            skLineSegment(sketch, "E149.top", {"start": v(12, 38.1) * mm, "end": v(15, 38.1) * mm});
            skLineSegment(sketch, "E149.left", {"start": v(12, 39.6) * mm, "end": v(12, 38.1) * mm});
            skLineSegment(sketch, "E149.right", {"start": v(15, 39.6) * mm, "end": v(15, 38.1) * mm});
            skLineSegment(sketch, "E150", {"start": v(30, 51.6) * mm, "end": v(30, 35.77) * mm, "construction": true});
            skLineSegment(sketch, "E151.MirrorCS", {"start": v(48, 39.6) * mm, "end": v(48, 38.1) * mm});
            skLineSegment(sketch, "E152.MirrorCS", {"start": v(45, 39.6) * mm, "end": v(45, 38.1) * mm});
            skLineSegment(sketch, "E153.MirrorCS", {"start": v(48, 39.6) * mm, "end": v(45, 39.6) * mm});
            skLineSegment(sketch, "E154.MirrorCS", {"start": v(48, 38.1) * mm, "end": v(45, 38.1) * mm});
            skSolve(sketch);
        }
        {
            var Q0;
            Q0=makeQuery(id+"F33.imprint","IMPRINT",FACE,{"disambiguationData":[TD([[makeQuery(id+"F33.imprint","IMPRINT",EDGE,{"derivedFrom":sQuery(id+"F33.wireOp",EDGE,"E149.bottom")}),-1.0]])]});
            var Q1;
            Q1=makeQuery(id+"F33.imprint","IMPRINT",FACE,{"disambiguationData":[TD([[makeQuery(id+"F33.imprint","IMPRINT",EDGE,{"derivedFrom":sQuery(id+"F33.wireOp",EDGE,"E151.MirrorCS")}),-1.0]])]});
            extrude(context, id + "F34", {"entities" : qUnion([Q0, Q1]), "operationType" : NewBodyOperationType.REMOVE, "endBound" : BoundingType.THROUGH_ALL, "oppositeDirection" : true, "depth" : 25 * mm});
        }
    });
